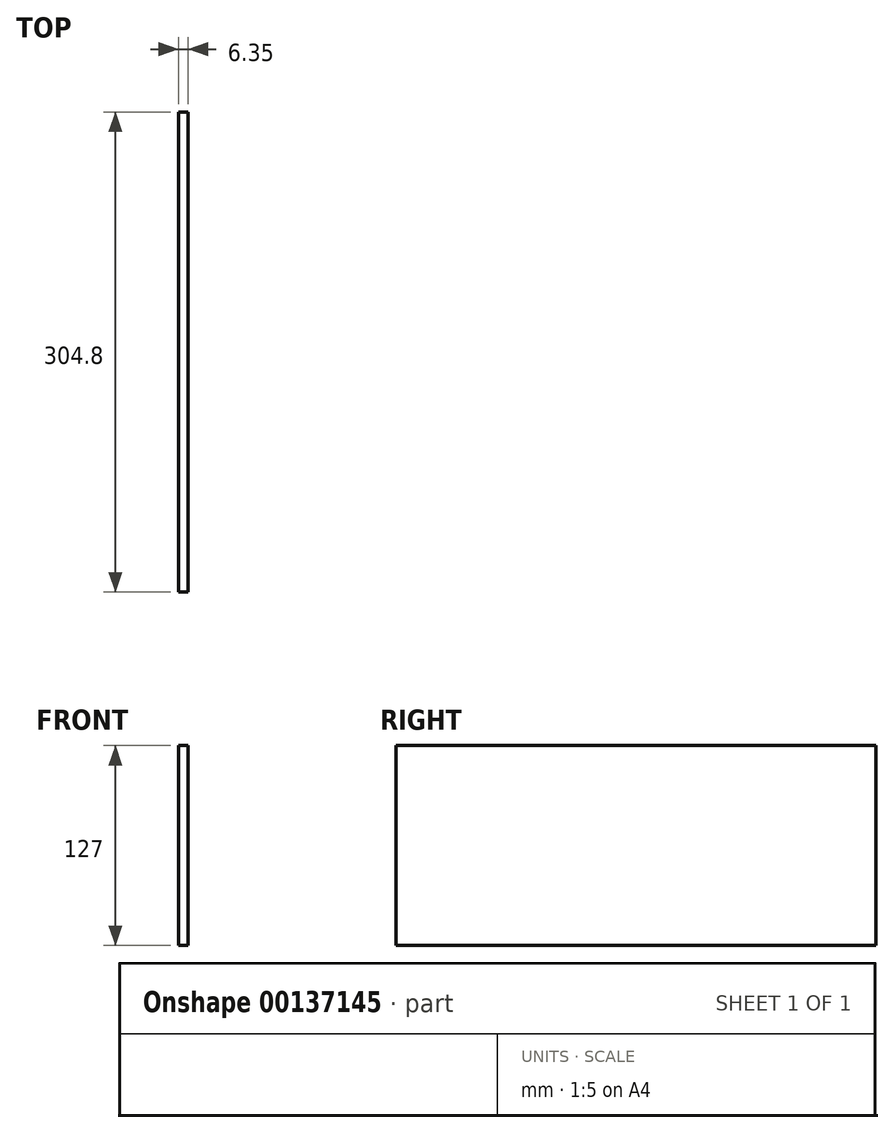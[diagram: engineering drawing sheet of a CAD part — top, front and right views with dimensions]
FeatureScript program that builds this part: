
annotation { "Feature Type Name" : "Feature", "Feature Type Description" : "" }
export const myFeature = defineFeature(function(context is Context, id is Id, definition is map)
    precondition{}
    {
        {
            var Q0;
            Q0=qCreatedBy(makeId("Right.planeOp"),FACE);
            var sketch = newSketch(context, id + "F0", { "sketchPlane" : qUnion([Q0])});
            skLineSegment(sketch, "E0.bottom", {"start": v(0, 0) * mm, "end": v(304.8, 0) * mm});
            skLineSegment(sketch, "E0.top", {"start": v(0, 127) * mm, "end": v(304.8, 127) * mm});
            skLineSegment(sketch, "E0.left", {"start": v(0, 0) * mm, "end": v(0, 127) * mm});
            skLineSegment(sketch, "E0.right", {"start": v(304.8, 0) * mm, "end": v(304.8, 127) * mm});
            skSolve(sketch);
        }
        {
            var Q0;
            Q0=makeQuery(id+"F0.imprint","IMPRINT",FACE,{"disambiguationData":[TD([[makeQuery(id+"F0.imprint","IMPRINT",EDGE,{"derivedFrom":sQuery(id+"F0.wireOp",EDGE,"E0.bottom")}),1.0]])]});
            extrude(context, id + "F1", {"entities" : qUnion([Q0]), "depth" : 6.35 * mm});
        }
    });
